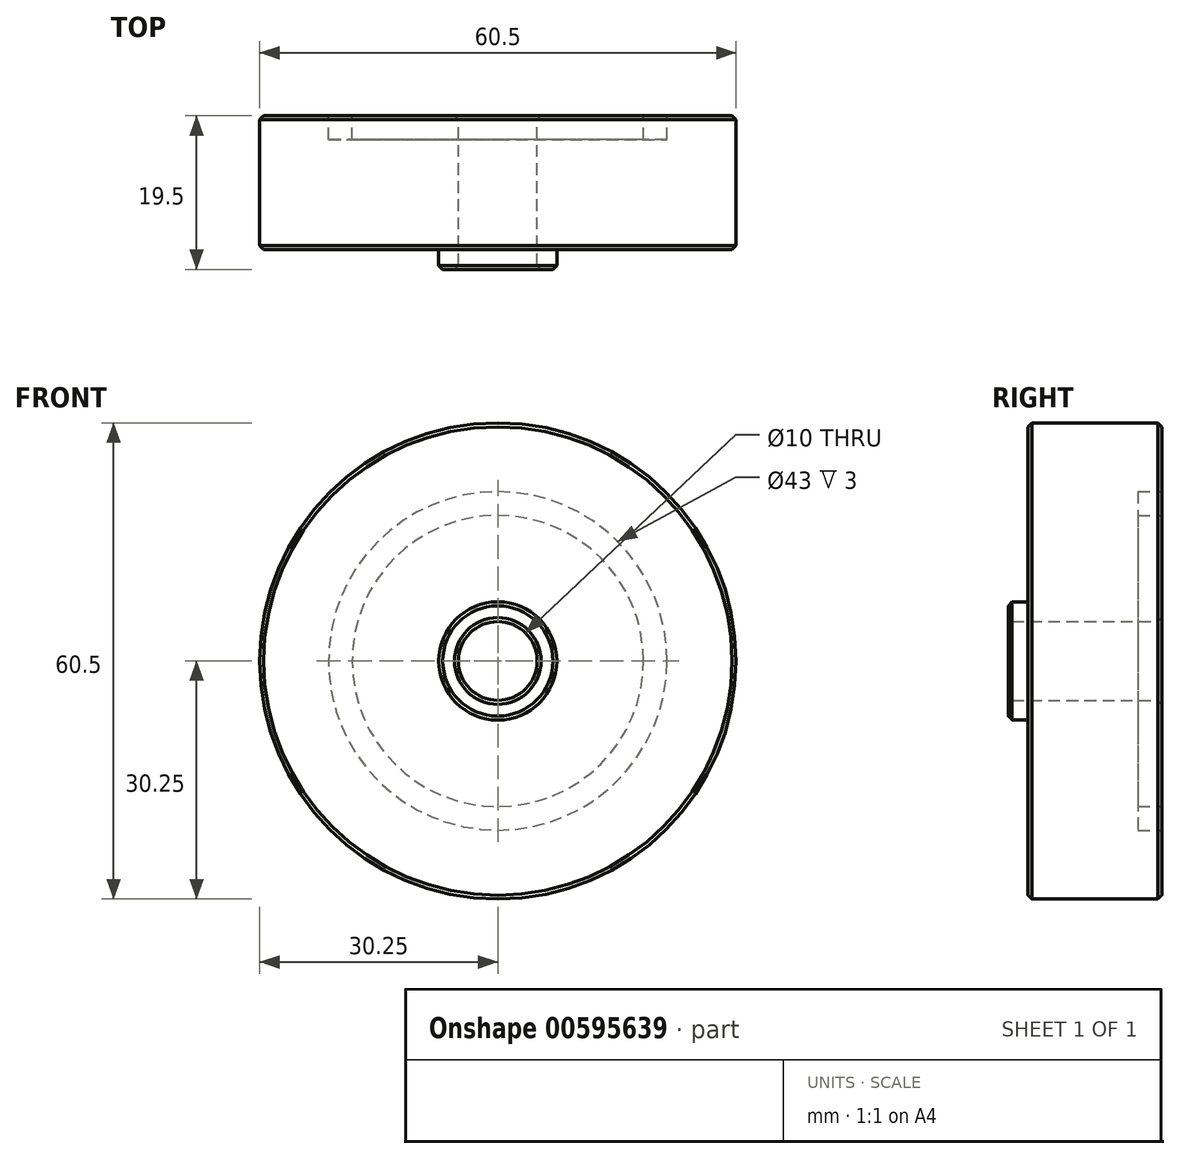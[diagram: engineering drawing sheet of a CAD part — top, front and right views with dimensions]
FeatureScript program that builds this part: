
annotation { "Feature Type Name" : "Feature", "Feature Type Description" : "" }
export const myFeature = defineFeature(function(context is Context, id is Id, definition is map)
    precondition{}
    {
        {
            var Q0;
            Q0=qCreatedBy(makeId("Front.planeOp"),FACE);
            var sketch = newSketch(context, id + "F0", { "sketchPlane" : qUnion([Q0])});
            skCircle(sketch, "E0", {"center": v(0, 0) * mm, "radius": 30.25 * mm});
            skCircle(sketch, "E1", {"center": v(0, 0) * mm, "radius": 5 * mm});
            skSolve(sketch);
        }
        {
            var Q0;
            Q0 = qSketchRegion(id + "F0", true);
            extrude(context, id + "F1", {"entities" : qUnion([Q0]), "depth" : 17 * mm, "offsetDistance" : 25 * mm});
        }
        {
            var Q0;
            Q0=makeQuery(id+"F1.opExtrude","CAP_FACE",FACE,{"disambiguationData":[OSD([sQuery(id+"F0.wireOp",EDGE,"E0"),sQuery(id+"F0.wireOp",EDGE,"E1")])],"isStart":false});
            var sketch = newSketch(context, id + "F2", { "sketchPlane" : qUnion([Q0])});
            skCircle(sketch, "E2", {"center": v(0, 0) * mm, "radius": 7.5 * mm});
            skCircle(sketch, "E3", {"center": v(0, 0) * mm, "radius": 5 * mm});
            skSolve(sketch);
        }
        {
            var Q0;
            Q0 = qSketchRegion(id + "F2", true);
            extrude(context, id + "F3", {"entities" : qUnion([Q0]), "operationType" : NewBodyOperationType.ADD, "depth" : 2.5 * mm, "offsetDistance" : 25 * mm});
        }
        {
            var Q0;
            Q0=makeQuery(id+"F1.opExtrude","CAP_FACE",FACE,{"disambiguationData":[OSD([sQuery(id+"F0.wireOp",EDGE,"E0"),sQuery(id+"F0.wireOp",EDGE,"E1")])],"isStart":true});
            var sketch = newSketch(context, id + "F4", { "sketchPlane" : qUnion([Q0])});
            skCircle(sketch, "E4", {"center": v(0, 0) * mm, "radius": 21.5 * mm});
            skCircle(sketch, "E5", {"center": v(0, 0) * mm, "radius": 18.5 * mm});
            skSolve(sketch);
        }
        {
            var Q0;
            Q0 = qSketchRegion(id + "F4", true);
            extrude(context, id + "F5", {"entities" : qUnion([Q0]), "operationType" : NewBodyOperationType.REMOVE, "oppositeDirection" : true, "depth" : 3 * mm, "offsetDistance" : 25 * mm});
        }
        {
            var Q0;
            Q0=makeQuery(id+"F1.opExtrude","CAP_EDGE",EDGE,{"disambiguationData":[OSD([sQuery(id+"F0.wireOp",EDGE,"E0")])],"isStart":false});
            var Q1;
            Q1=makeQuery(id+"F3.opExtrude","CAP_EDGE",EDGE,{"disambiguationData":[OSD([sQuery(id+"F2.wireOp",EDGE,"E2")])],"isStart":false});
            var Q2;
            Q2=makeQuery(id+"F3.opExtrude","CAP_FACE",FACE,{"disambiguationData":[OSD([sQuery(id+"F2.wireOp",EDGE,"E2"),sQuery(id+"F2.wireOp",EDGE,"E3")])],"isStart":false});
            var Q3;
            Q3=makeQuery(id+"F1.opExtrude","CAP_EDGE",EDGE,{"disambiguationData":[OSD([sQuery(id+"F0.wireOp",EDGE,"E0")])],"isStart":true});
            var Q4;
            Q4=makeQuery(id+"F1.opExtrude","CAP_EDGE",EDGE,{"disambiguationData":[OSD([sQuery(id+"F0.wireOp",EDGE,"E1")])],"isStart":true});
            chamfer(context, id + "F6", {"entities" : qUnion([Q0, Q1, Q2, Q3, Q4]), "width" : .5 * mm, "tangentPropagation" : true});
        }
    });
